# Revit family: PRE070015-FR
name_source: partatom
category: Accessoire de canalisation
revit_build: Autodesk Revit 2017 (Build: 20160225_1515(x64)
units: mm (PartAtom-declared; Revit-internal decimal feet)

## family parameters
Basée sur le plan de construction = Non
Cote de connecteur circulaire = Utiliser le diamètre
Couper avec des vides une fois chargée = Non
Partagée = Non
Toujours verticalement = Oui
Type d'élément = Normal

## types (4) — shared parameters
Adresse = 7, RUE RACINE - 92542 MONTROUGE CEDEX FRANCE
Diamètre Nominal = 12 mm  [stored 0.0393701 ft]
Fabricant = LES ROBINETS PRESTO S.A.
Flux = 0.1 L/s
Garantie = 3
Hauteur = 177 mm  [stored 0.580709 ft]
LC = 23 mm
Largeur = 51 mm  [stored 0.167323 ft]
Lien CCTP = http://www.prestodatashare.com
Lien fiche produit = http://www.prestodatashare.com
Lien notice d'utilisation = http://www.prestodatashare.com
Matériau = Laiton poli chromé
PC = 23 mm
Perte de charge = 0.0 Pa
Pression = 1 à 5 bars
Profondeur = 207 mm  [stored 0.679134 ft]
Raccordement = G 3/8'' (12x17)
URL = http://www.prestodatashare.com
URL Fabricant = http://www.prestodatashare.com
Variantes = 55379-55381-55389-55393

## per-type parameters (varying)
| type | Debit | Description | Fonction | Polantis code | Reference |
| 55381 PRESTO NOVA SIMPLE PILE PRESTOGREEN | 1,9 l/mn | Robinet simple sur plage à détection (CE) sur plage. De type Presto NOVA® réf. 55381 ou techniquement équivalent. Avec cellule optoélectronique, alimentation par pile lithium 6 V intégrée dans le robinet. Limiteur de débit intégré 1,9 l/mn). Système antiblocage interdisant l'écoulement en continu. Avec flexible PEX et robinet d’arrêt filtre. Finition chromée. | Débit : 1,9 l/mn par limiteur de débit intégré, Aérateur anti-tartre haute qualité, Dispositif anti-coup de bélier
Alimentation électrique : Pile lithium 6 volts type CRP2 dans boîtier intégré dans le corps du robinet
Matière et couleur de finition : Corps et capot en métal moulé injecté avec finition chromée
Résistance thermique : Résiste à une température de 75°C durant 30 minutes dans le cadre de chocs thermiques
Sécurité : Limitation de la température maximale par butée réglable
-Fermeture automatique de l'électrovanne en cas d'écoulement > à 30s, d'usure de la pile ou de dégradation du détecteur

Livré avec :
- 1 Ecrou de fixation
- 1 Joint et 1 rondelle
- 1 Flexible PEX à écrou tournant avec Clapets anti-retour NF
- 1 Robinet d'arrêt MM G 3/8'' (12x17)
- 1 Joint filtre
- 1 Autocollant de signalisation

Normes / Agréments :
- Laiton conforme aux normes NF EN1982, EN12164, NF EN12165
- Résistant au brouillard salin 200 H (essai NSS) conformément à la norme NF ISO 9227 | PRE070015a | 55381 |
| 55379 PRESTO NOVA SIMPLE PILE | 3 l/mn | Robinet simple sur plage à détection (CE) sur plage. De type Presto NOVA® réf. 55379 ou techniquement équivalent. Avec cellule optoélectronique, alimentation par pile lithium 6 V intégrée dans le robinet. Régulateur de débit intégré (3 l/min).Système antiblocage interdisant l'écoulement en continu. Avec flexible PEX et robinet d’arrêt filtre. Finition chromée | Débit : 3 l/mn par limiteur de débit intégré, Aérateur anti-tartre haute qualité, Dispositif anti-coup de bélier
Alimentation électrique : Pile lithium 6 volts type CRP2 dans boîtier intégré dans le corps du robinet
Matière et couleur de finition : Corps et capot en métal moulé injecté avec finition chromée
Résistance thermique : Résiste à une température de 75°C durant 30 minutes dans le cadre de chocs thermiques
Sécurité : Limitation de la température maximale par butée réglable
-Fermeture automatique de l'électrovanne en cas d'écoulement > à 30s, d'usure de la pile ou de dégradation du détecteur

Livré avec :
- 1 Ecrou de fixation
- 1 Joint et 1 rondelle
- 1 Flexible PEX à écrou tournant avec Clapets anti-retour NF
- 1 Robinet d'arrêt MM G 3/8'' (12x17)
- 1 Joint filtre
- 1 Autocollant de signalisation

Normes / Agréments :
- Laiton conforme aux normes NF EN1982, EN12164, NF EN12165
- Résistant au brouillard salin 200 H (essai NSS) conformément à la norme NF ISO 9227 | PRE070015 | 55379 |
| 55393 PRESTO SIMPLE NOVA BLACK CHROME PILE | 3 l/mn | Robinet simple sur plage à détection (CE) sur plage. De type Presto NOVA® réf. 55393 ou techniquement équivalent. Avec cellule optoélectronique, alimentation par pile lithium 6 V intégrée dans le robinet. Régulateur de débit intégré (3 l/min).Système antiblocage interdisant l'écoulement en continu. Avec flexible PEX et robinet d’arrêt filtre. Finition corps chromé et capot BLACK CHROME | Débit : 3 l/mn par limiteur de débit intégré, Aérateur anti-tartre haute qualité, Dispositif anti-coup de bélier
Alimentation électrique : Pile lithium 6 volts type CRP2 dans boîtier intégré dans le corps du robinet
Matière et couleur de finition : Corps et capot en métal moulé injecté avec finition black chrome
Résistance thermique : Résiste à une température de 75°C durant 30 minutes dans le cadre de chocs thermiques
Sécurité : Limitation de la température maximale par butée réglable
-Fermeture automatique de l'électrovanne en cas d'écoulement > à 30s, d'usure de la pile ou de dégradation du détecteur

Livré avec :
- 1 Ecrou de fixation
- 1 Joint et 1 rondelle
- 1 Flexible PEX à écrou tournant avec Clapets anti-retour NF
- 1 Robinet d'arrêt MM G 3/8'' (12x17)
- 1 Joint filtre
- 1 Autocollant de signalisation

Normes / Agréments :
- Laiton conforme aux normes NF EN1982, EN12164, NF EN12165
- Résistant au brouillard salin 200 H (essai NSS) conformément à la norme NF ISO 9227 | PRE070015c | 55393 |
| 55389 PRESTO NOVA SIMPLE  NOIR MAT PILE | 3 l/mn | Robinet simple sur plage à détection (CE) sur plage. De type Presto NOVA® réf. 55389 ou techniquement équivalent. Avec cellule optoélectronique, alimentation par pile lithium 6 V intégrée dans le robinet. Régulateur de débit intégré (3 l/min).Système antiblocage interdisant l'écoulement en continu. Avec flexible PEX et robinet d’arrêt filtre. Finition NOIR MAT | Débit : 3 l/mn par limiteur de débit intégré, Aérateur anti-tartre haute qualité, Dispositif anti-coup de bélier
Alimentation électrique : Pile lithium 6 volts type CRP2 dans boîtier intégré dans le corps du robinet
Matière et couleur de finition : Corps et capot en métal moulé injecté avec finition noir mat
Résistance thermique : Résiste à une température de 75°C durant 30 minutes dans le cadre de chocs thermiques
Sécurité : Limitation de la température maximale par butée réglable
-Fermeture automatique de l'électrovanne en cas d'écoulement > à 30s, d'usure de la pile ou de dégradation du détecteur

Livré avec :
- 1 Ecrou de fixation
- 1 Joint et 1 rondelle
- 1 Flexible PEX à écrou tournant avec Clapets anti-retour NF
- 1 Robinet d'arrêt MM G 3/8'' (12x17)
- 1 Joint filtre
- 1 Autocollant de signalisation

Normes / Agréments :
- Laiton conforme aux normes NF EN1982, EN12164, NF EN12165
- Résistant au brouillard salin 200 H (essai NSS) conformément à la norme NF ISO 9227 | PRE070015b | 55389 |

note: column(s) folded — value = type name in every type: Modèle

note: [stored X ft] marks values corroborated as IEEE doubles in the binary element streams (Revit-internal decimal feet)
